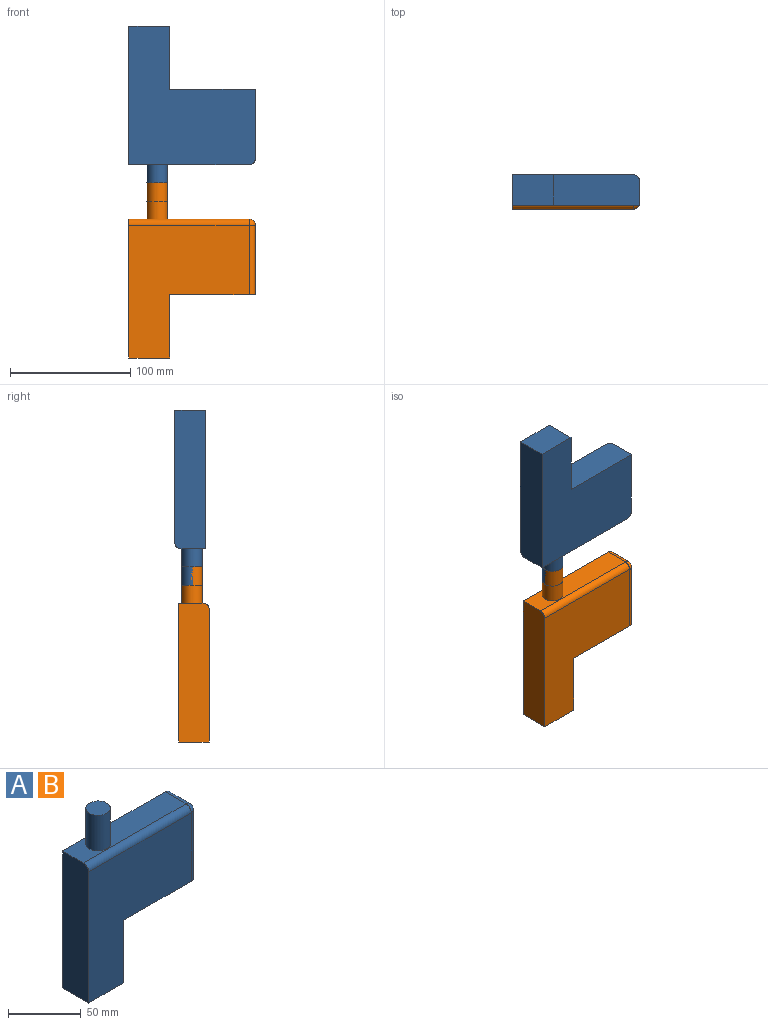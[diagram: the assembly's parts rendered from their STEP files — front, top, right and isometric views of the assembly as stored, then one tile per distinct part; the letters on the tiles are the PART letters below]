
ASSEMBLY  parts=2 mates=1
PART A: 14 faces, bbox 105x25.4x145.5 mm
  f0: plane 99.94x20.32mm, normal (0,0,1), area 1802.8mm2, adj f1,f7,f8,f11,f13
  f1: plane 115.45x25.4mm, normal (-1,0,0), area 2926.9mm2, adj f0,f2,f6,f7,f11
  f2: plane 33.98x25.4mm, normal (0,0,-1), area 863mm2, adj f1,f3,f6,f7
  f3: plane 52.74x25.4mm, normal (1,0,0), area 1339.7mm2, adj f2,f4,f6,f7
  f4: plane 71.04x25.4mm, normal (0,0,-1), area 1798.9mm2, adj f3,f5,f6,f7,f10
  f5: plane 57.63x20.32mm, normal (1,0,0), area 1171mm2, adj f4,f7,f10,f13
  f6: plane 110.37x99.94mm, normal (0,-1,0), area 7551.2mm2, adj f1,f2,f3,f4,f10,f11
  f7: plane 115.45x105.02mm, normal (0,1,0), area 8371.9mm2, adj f0,f1,f2,f3,f4,f5,f13
  f8: cylinder r=8.52mm len=30mm, axis (0,0,-1), area 1605.5mm2, adj f0,f9
  f9: plane 17.04x17.04mm, normal (0,0,1), area 227.9mm2, adj f8
  f10: cylinder r=5.08mm len=57.63mm, axis (0,0,-1), area 459.9mm2, adj f4,f5,f6,f12
  f11: cylinder r=5.08mm len=99.94mm, axis (1,0,0), area 797.5mm2, adj f0,f1,f6,f12
  f12: sphere r=5.08mm, area 40.5mm2, adj f10,f11,f13
  f13: cylinder r=5.08mm len=20.32mm, axis (0,1,0), area 162.1mm2, adj f0,f5,f7,f12
PART B: same geometry as A
PLACE A rot(axis=(1,0,0),180deg) t=(27.96,-39.85,194.19)mm
PLACE B t=(27.96,-17.5,42.08)mm
MATE revolute A.f8 <-> B.f8  axis (0,0,1) through (-79.61,-28.68,110.64)mm
